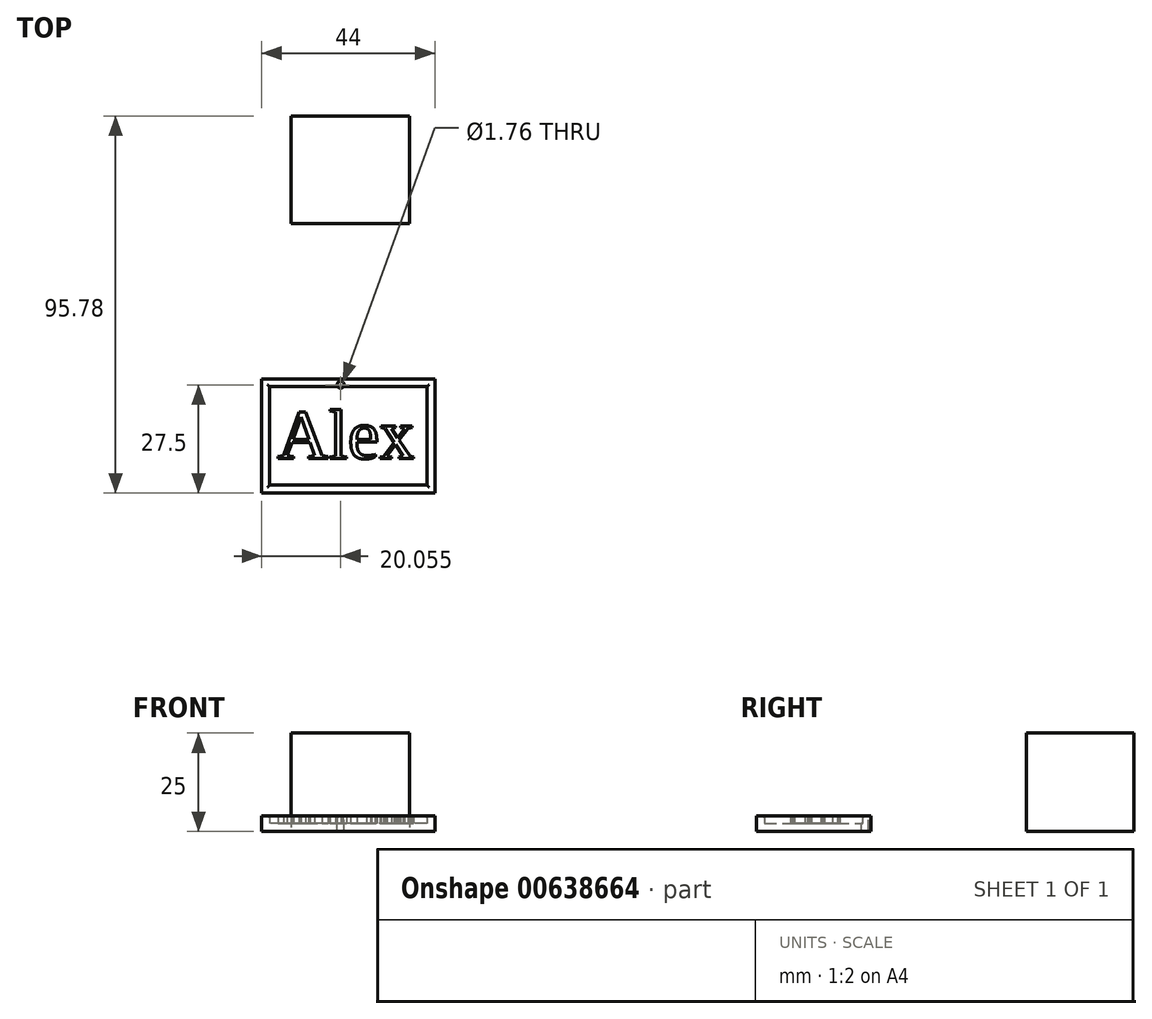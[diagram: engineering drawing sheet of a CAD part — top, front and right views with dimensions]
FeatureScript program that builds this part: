
annotation { "Feature Type Name" : "Feature", "Feature Type Description" : "" }
export const myFeature = defineFeature(function(context is Context, id is Id, definition is map)
    precondition{}
    {
        {
            var Q0;
            Q0=qCreatedBy(makeId("Top.planeOp"),FACE);
            var sketch = newSketch(context, id + "F0", { "sketchPlane" : qUnion([Q0])});
            skLineSegment(sketch, "E0.bottom", {"start": v(20, -12.5) * mm, "end": v(-20, -12.5) * mm});
            skLineSegment(sketch, "E0.top", {"start": v(20, 12.5) * mm, "end": v(-20, 12.5) * mm});
            skLineSegment(sketch, "E0.left", {"start": v(20, -12.5) * mm, "end": v(20, 12.5) * mm});
            skLineSegment(sketch, "E0.right", {"start": v(-20, -12.5) * mm, "end": v(-20, 12.5) * mm});
            skPoint(sketch, "E0.middle", {"position": v(0, 0) * mm});
            skSolve(sketch);
        }
        {
            var Q0;
            Q0=makeQuery(id+"F0.imprint","IMPRINT",FACE,{"disambiguationData":[TD([[makeQuery(id+"F0.imprint","IMPRINT",EDGE,{"derivedFrom":sQuery(id+"F0.wireOp",EDGE,"E0.bottom")}),-1.0]])]});
            var sketch = newSketch(context, id + "F1", { "sketchPlane" : qUnion([Q0])});
            skLineSegment(sketch, "E1.0", {"start": v(22, 14.5) * mm, "end": v(-22, 14.5) * mm});
            skLineSegment(sketch, "E1.1", {"start": v(22, -14.5) * mm, "end": v(22, 14.5) * mm});
            skLineSegment(sketch, "E1.2", {"start": v(22, -14.5) * mm, "end": v(-22, -14.5) * mm});
            skLineSegment(sketch, "E1.3", {"start": v(-22, -14.5) * mm, "end": v(-22, 14.5) * mm});
            skSolve(sketch);
        }
        {
            var Q0;
            Q0=makeQuery(id+"F1.imprint","IMPRINT",FACE,{"disambiguationData":[TD([[makeQuery(id+"F1.imprint","IMPRINT",EDGE,{"derivedFrom":sQuery(id+"F1.wireOp",EDGE,"E1.0")}),1.0]])]});
            extrude(context, id + "F2", {"entities" : qUnion([Q0]), "depth" : 4 * mm, "offsetDistance" : 25 * mm});
        }
        {
            var Q0;
            Q0=makeQuery(id+"F0.imprint","IMPRINT",FACE,{"disambiguationData":[TD([[makeQuery(id+"F0.imprint","IMPRINT",EDGE,{"derivedFrom":sQuery(id+"F0.wireOp",EDGE,"E0.bottom")}),-1.0]])]});
            extrude(context, id + "F3", {"entities" : qUnion([Q0]), "operationType" : NewBodyOperationType.ADD, "depth" : 2 * mm, "offsetDistance" : 25 * mm});
        }
        {
            var Q0;
            Q0=makeQuery(id+"F2.opExtrude","CAP_EDGE",EDGE,{"disambiguationData":[OSD([sQuery(id+"F0.wireOp",EDGE,"E0.top")])],"isStart":false});
            var Q1;
            Q1=makeQuery(id+"F2.opExtrude","CAP_EDGE",EDGE,{"disambiguationData":[OSD([sQuery(id+"F0.wireOp",EDGE,"E0.right")])],"isStart":false});
            var Q2;
            Q2=makeQuery(id+"F2.opExtrude","CAP_EDGE",EDGE,{"disambiguationData":[OSD([sQuery(id+"F0.wireOp",EDGE,"E0.bottom")])],"isStart":false});
            var Q3;
            Q3=makeQuery(id+"F2.opExtrude","CAP_EDGE",EDGE,{"disambiguationData":[OSD([sQuery(id+"F0.wireOp",EDGE,"E0.left")])],"isStart":false});
            fillet(context, id + "F4", {"entities" : qUnion([Q0, Q1, Q2, Q3]), "radius" : 0.5 * mm, "tangentPropagation" : true, "allowEdgeOverflow" : false});
        }
        {
            var Q0;
            Q0=makeQuery(id+"F3.opExtrude","CAP_FACE",FACE,{"disambiguationData":[OSD([sQuery(id+"F0.wireOp",EDGE,"E0.bottom"),sQuery(id+"F0.wireOp",EDGE,"E0.top"),sQuery(id+"F0.wireOp",EDGE,"E0.left"),sQuery(id+"F0.wireOp",EDGE,"E0.right")])],"isStart":false});
            var sketch = newSketch(context, id + "F5", { "sketchPlane" : qUnion([Q0])});
            skText(sketch, "E2", { "text": "Alex", "fontName": "Tinos-Regular.ttf"});
            const initialGuessF5  = {"E2": [-0.01797, -0.00573, 1, 0, 0.01288]};
            skSetInitialGuess(sketch, initialGuessF5);
            skSolve(sketch);
        }
        {
            var Q0;
            Q0 = qSketchRegion(id + "F5", true);
            extrude(context, id + "F6", {"entities" : qUnion([Q0]), "operationType" : NewBodyOperationType.ADD, "depth" : 2 * mm, "offsetDistance" : 25 * mm});
        }
        {
            var Q0;
            Q0=makeQuery(id+"F2.opExtrude","CAP_FACE",FACE,{"disambiguationData":[OSD([sQuery(id+"F0.wireOp",EDGE,"E0.bottom"),sQuery(id+"F0.wireOp",EDGE,"E0.top"),sQuery(id+"F0.wireOp",EDGE,"E0.left"),sQuery(id+"F0.wireOp",EDGE,"E0.right"),sQuery(id+"F1.wireOp",EDGE,"E1.0"),sQuery(id+"F1.wireOp",EDGE,"E1.1"),sQuery(id+"F1.wireOp",EDGE,"E1.2"),sQuery(id+"F1.wireOp",EDGE,"E1.3")])],"isStart":false});
            var sketch = newSketch(context, id + "F7", { "sketchPlane" : qUnion([Q0])});
            skCircle(sketch, "E3", {"center": v(-1.94, 13) * mm, "radius": 0.88 * mm});
            skSolve(sketch);
        }
        {
            var Q0;
            Q0 = qSketchRegion(id + "F7", true);
            extrude(context, id + "F8", {"entities" : qUnion([Q0]), "operationType" : NewBodyOperationType.REMOVE, "oppositeDirection" : true, "depth" : 25 * mm, "offsetDistance" : 25 * mm});
        }
        {
            var Q0;
            Q0=qCreatedBy(makeId("Top.planeOp"),FACE);
            var sketch = newSketch(context, id + "F9", { "sketchPlane" : qUnion([Q0])});
            skLineSegment(sketch, "E4.bottom", {"start": v(-14.6, 81.28) * mm, "end": v(15.5, 81.28) * mm});
            skLineSegment(sketch, "E4.top", {"start": v(-14.6, 53.98) * mm, "end": v(15.5, 53.98) * mm});
            skLineSegment(sketch, "E4.left", {"start": v(-14.6, 81.28) * mm, "end": v(-14.6, 53.98) * mm});
            skLineSegment(sketch, "E4.right", {"start": v(15.5, 81.28) * mm, "end": v(15.5, 53.98) * mm});
            skSolve(sketch);
        }
        {
            var Q0;
            Q0=makeQuery(id+"F9.imprint","IMPRINT",FACE,{"disambiguationData":[TD([[makeQuery(id+"F9.imprint","IMPRINT",EDGE,{"derivedFrom":sQuery(id+"F9.wireOp",EDGE,"E4.bottom")}),-1.0]])]});
            extrude(context, id + "F10", {"entities" : qUnion([Q0]), "depth" : 25 * mm, "offsetDistance" : 25 * mm});
        }
    });
